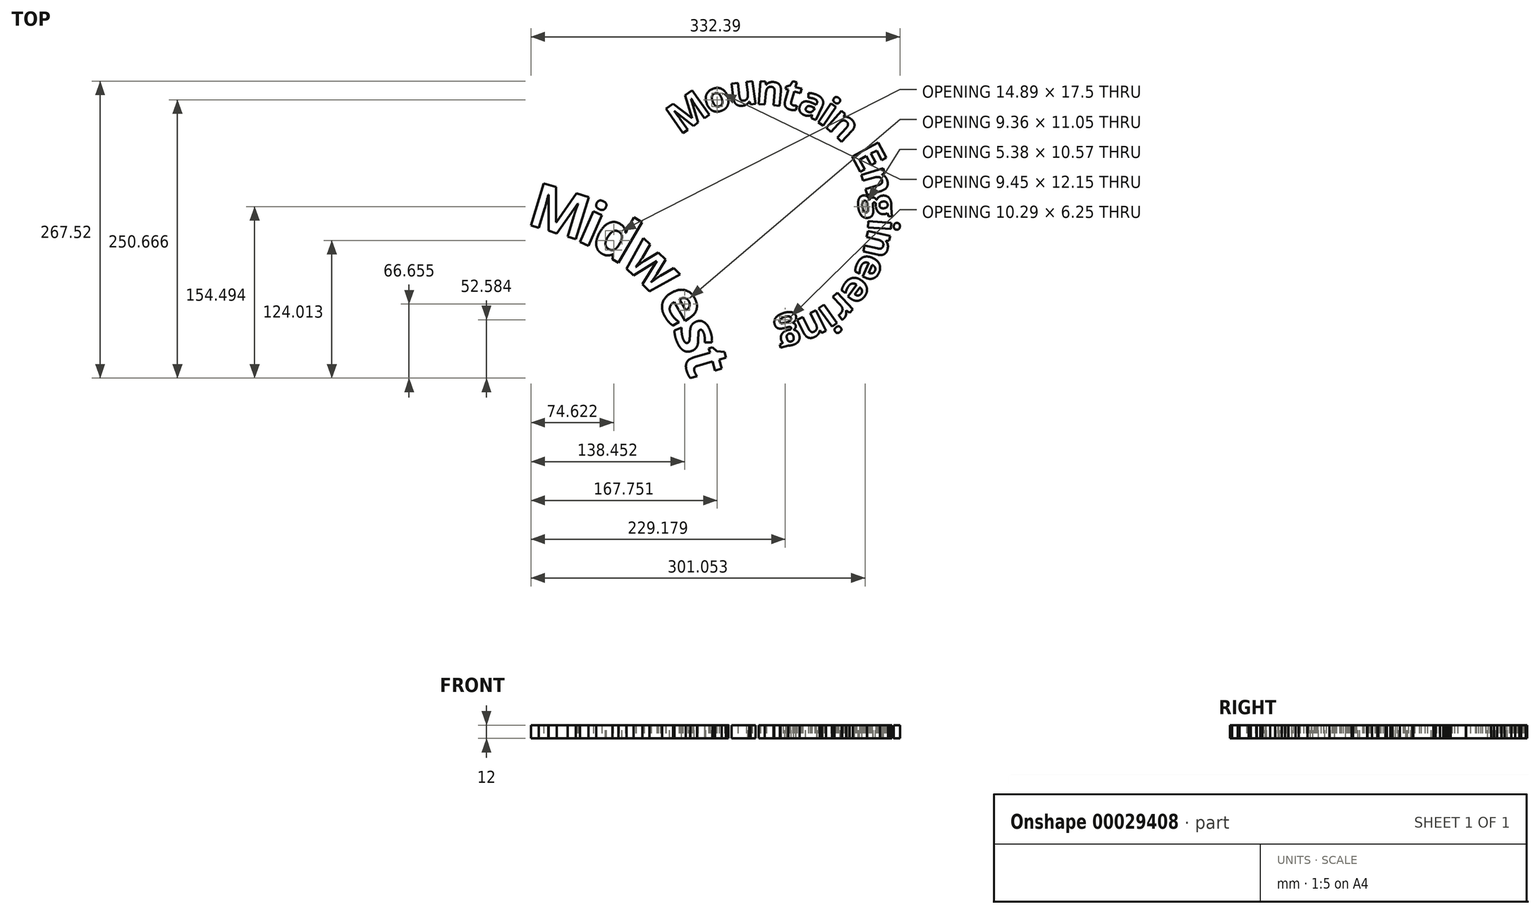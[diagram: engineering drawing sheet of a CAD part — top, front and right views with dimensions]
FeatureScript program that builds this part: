
annotation { "Feature Type Name" : "Feature", "Feature Type Description" : "" }
export const myFeature = defineFeature(function(context is Context, id is Id, definition is map)
    precondition{}
    {
        {
            var Q0;
            Q0=qCreatedBy(makeId("Top.planeOp"),FACE);
            var sketch = newSketch(context, id + "F0", { "sketchPlane" : qUnion([Q0])});
            skText(sketch, "E0", { "text": "M", "fontName": "OpenSans-Bold.ttf"});
            skText(sketch, "E1", { "text": "i", "fontName": "OpenSans-Bold.ttf"});
            skText(sketch, "E2", { "text": "d", "fontName": "OpenSans-Bold.ttf"});
            skText(sketch, "E3", { "text": "w", "fontName": "OpenSans-Bold.ttf"});
            skText(sketch, "E4", { "text": "e", "fontName": "OpenSans-Bold.ttf"});
            skText(sketch, "E5", { "text": "s", "fontName": "OpenSans-Bold.ttf"});
            skText(sketch, "E6", { "text": "t", "fontName": "OpenSans-Bold.ttf"});
            skText(sketch, "E7", { "text": "o", "fontName": "OpenSans-Bold.ttf"});
            skText(sketch, "E8", { "text": "u", "fontName": "OpenSans-Bold.ttf"});
            skText(sketch, "E9", { "text": "n", "fontName": "OpenSans-Bold.ttf"});
            skText(sketch, "E10", { "text": "M", "fontName": "OpenSans-Bold.ttf"});
            skText(sketch, "E11", { "text": "t", "fontName": "OpenSans-Bold.ttf"});
            skText(sketch, "E12", { "text": "a", "fontName": "OpenSans-Bold.ttf"});
            skText(sketch, "E13", { "text": "i", "fontName": "OpenSans-Bold.ttf"});
            skText(sketch, "E14", { "text": "n", "fontName": "OpenSans-Bold.ttf"});
            skText(sketch, "E15", { "text": "E", "fontName": "OpenSans-Bold.ttf"});
            skText(sketch, "E16", { "text": "n", "fontName": "OpenSans-Bold.ttf"});
            skText(sketch, "E17", { "text": "g", "fontName": "OpenSans-Bold.ttf"});
            skText(sketch, "E18", { "text": "i", "fontName": "OpenSans-Bold.ttf"});
            skText(sketch, "E19", { "text": "n", "fontName": "OpenSans-Bold.ttf"});
            skText(sketch, "E20", { "text": "e", "fontName": "OpenSans-Bold.ttf"});
            skText(sketch, "E21", { "text": "e", "fontName": "OpenSans-Bold.ttf"});
            skText(sketch, "E22", { "text": "r", "fontName": "OpenSans-Bold.ttf"});
            skText(sketch, "E23", { "text": "i", "fontName": "OpenSans-Bold.ttf"});
            skText(sketch, "E24", { "text": "n", "fontName": "OpenSans-Bold.ttf"});
            skText(sketch, "E25", { "text": "g", "fontName": "OpenSans-Bold.ttf"});
            skFitSpline(sketch, "E26", {"points": [v(-509.02, -128.55) * mm, v(-114.69, -51.63) * mm, v(0, -335.04) * mm, v(145.58, -82.27) * mm], "startDerivative": vector(-305.8, 1050.7) * mm, "endDerivative": vector(-1254.4, 814.2) * mm});
            skLineSegment(sketch, "E27", {"start": v(-169.02, -34.57) * mm, "end": v(-164.03, -22.38) * mm, "construction": true});
            skLineSegment(sketch, "E28", {"start": v(-157.85, -39.52) * mm, "end": v(-152.16, -27.63) * mm, "construction": true});
            skLineSegment(sketch, "E29", {"start": v(-125.6, -43.1) * mm, "end": v(-117.98, -32.35) * mm, "construction": true});
            skLineSegment(sketch, "E30", {"start": v(-92.64, -75.72) * mm, "end": v(-81.97, -68) * mm, "construction": true});
            skLineSegment(sketch, "E31", {"start": v(-77.26, -101.84) * mm, "end": v(-65.37, -96.17) * mm, "construction": true});
            skLineSegment(sketch, "E32", {"start": v(-55.27, -121.23) * mm, "end": v(-67.75, -125.45) * mm, "construction": true});
            const initialGuessF0  = {"E0": [-0.20895, -0.00754, 0.95623, -0.29261, 0.04], "E1": [-0.164, -0.02229, 0.91448, -0.40462, 0.04], "E2": [-0.15189, -0.02707, 0.86515, -0.50152, 0.04], "E3": [-0.12446, -0.04149, 0.71037, -0.70383, 0.04], "E4": [-0.09206, -0.0753, 0.50596, -0.86256, 0.04], "E5": [-0.0769, -0.10167, 0.37247, -0.92804, 0.04], "E6": [-0.06753, -0.12538, 0.28003, -0.96, 0.04], "E7": [-0.04391, 0.09049, 0.94134, 0.33746, 0.02708], "E8": [-0.02358, 0.09779, 0.9918, 0.1278, 0.02708], "E9": [-0.00198, 0.10058, 0.99601, -0.08924, 0.02708], "E10": [-0.06986, 0.07226, 0.82069, 0.57138, 0.02708], "E11": [0.01977, 0.09832, 0.96274, -0.27042, 0.02708], "E12": [0.0344, 0.09443, 0.90115, -0.43352, 0.02708], "E13": [0.0521, 0.08546, 0.83012, -0.55759, 0.02708], "E14": [0.0597, 0.08096, 0.73545, -0.67758, 0.02708], "E15": [0.08348, 0.05585, 0.47567, -0.87962, 0.02708], "E16": [0.09259, 0.03934, 0.2886, -0.95745, 0.02708], "E17": [0.09885, 0.01837, 0.07995, -0.9968, 0.02708], "E18": [0.10007, -0.00237, -0.06756, -0.99772, 0.02708], "E19": [0.09997, -0.0112, -0.21883, -0.97576, 0.02708], "E20": [0.09512, -0.03254, -0.41897, -0.908, 0.02708], "E21": [0.08648, -0.05125, -0.5953, -0.8035, 0.02708], "E22": [0.07407, -0.06768, -0.73224, -0.68105, 0.02708], "E23": [0.062, -0.07859, -0.81158, -0.58425, 0.02708], "E24": [0.05513, -0.08415, -0.89114, -0.45374, 0.02708], "E25": [0.0356, -0.09403, -0.96684, -0.25537, 0.02708]};
            skSetInitialGuess(sketch, initialGuessF0);
            skSolve(sketch);
        }
        {
            var Q0;
            Q0=qSketchRegion(id+"F0",true);
            extrude(context, id + "F1", {"entities" : qUnion([Q0]), "depth" : 10 * mm, "hasSecondDirection" : true, "secondDirectionOppositeDirection" : true, "secondDirectionDepth" : 2 * mm});
        }
    });
